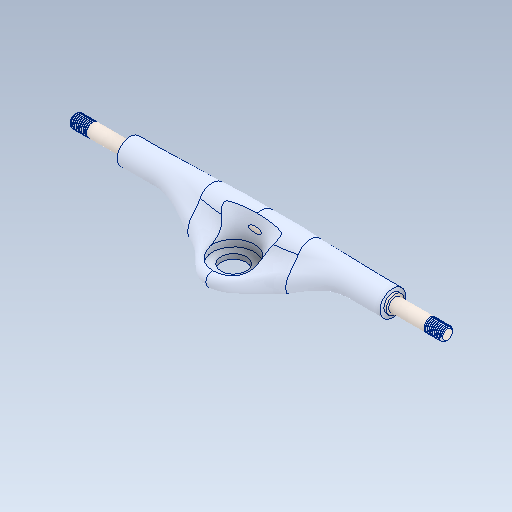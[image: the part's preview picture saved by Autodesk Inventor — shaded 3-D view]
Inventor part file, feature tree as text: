
AUTODESK INVENTOR PART (.ipt)
format: ipt  version: 2021 (Build 250183000, 183)  size: 674,816 bytes
history: mixed  units: in
note: dims shown in document units (in); Inventor stores cm internally (conversion verified against a paired STEP export)
features: thread x1, imported_body x1
ambient origin geometry x8: Origin, YZ Plane, XZ Plane, XY Plane, X Axis, Y Axis, Z Axis, Center Point
bodies: Solid1 (imported_parasolid)
feature tree (2):
  thread  "Thread2"  [1 undecoded]
  imported_body  NMx_Import_Brep_tag  [imported B-rep: ~6 faces, bbox_mm=None]
note: 1 required parameter value undecoded (feature->parameter linkage not recoverable at this tier; creation-order binding heuristic only, values carry confidence <= 0.55)
